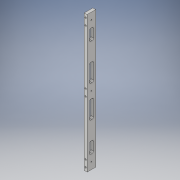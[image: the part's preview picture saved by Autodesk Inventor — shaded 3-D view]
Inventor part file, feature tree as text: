
AUTODESK INVENTOR PART (.ipt)
format: ipt  version: 2019 (Build 230136000, 136)  size: 211,456 bytes
history: native  units: in
note: dims shown in document units (in); Inventor stores cm internally (conversion verified against a paired STEP export)
features: fillet x16, sketch x4, extrude x2, hole x2
ambient origin geometry x8: Origin, YZ Plane, XZ Plane, XY Plane, X Axis, Y Axis, Z Axis, Center Point
bodies: Solid1 (feature_tree)
feature tree (24):
  extrude  "Extrusion1"  Depth=0.75in
  hole  "Hole1"  [1 undecoded]
  extrude  "Extrusion2"  Depth=5.9055in
  fillet  "Fillet1"  Radius=0.5906in
  fillet  "Fillet2"  Radius=0.375in
  fillet  "Fillet3"  Radius=0.375in
  fillet  "Fillet4"  Radius=5.9055in
  fillet  "Fillet5"  Radius=0.1969in
  fillet  "Fillet6"  Radius=0.1969in
  fillet  "Fillet7"  Radius=1.1811in
  fillet  "Fillet8"  Radius=1.1811in
  fillet  "Fillet9"  Radius=2.1654in
  fillet  "Fillet10"  Radius=3.7402in
  fillet  "Fillet11"  Radius=5.315in
  fillet  "Fillet12"  Radius=2.1654in
  fillet  "Fillet13"  Radius=3.7402in
  fillet  "Fillet14"  Radius=5.315in
  fillet  "Fillet15"  Radius=0.25in
  fillet  "Fillet16"  Radius=0.125in
  hole  "Hole3"  [1 undecoded]
  sketch  "Sketch1"  dims[d0=11.811in d1=0.75in]
  sketch  "Sketch2"  dims[d2=0.25in d3=0.0in d4=0.5906in]
  sketch  "Sketch5"  dims[d5=0.75in d6=0.375in d7=0.5906in d8=0.375in d9=0.375in d10=5.9055in]
  sketch  "Sketch7"  dims[d11=0.097in d12=0.236in d13=0.375in d14=0.25in d15=0.5635in d16=0.346in d17=0.8108in d44=0.1969in d45=0.1969in d46=1.1811in d47=1.1811in d48=2.1654in d49=3.7402in d50=5.315in d51=2.1654in d52=3.7402in d53=5.315in d54=0.25in d55=0.0in d56=0.125in d57=0.125in d58=0.125in d59=0.125in d60=0.125in d61=0.125in d62=0.125in d63=0.125in d64=0.125in d65=0.125in d66=0.125in d67=0.125in d68=0.125in d69=0.125in d70=0.125in d71=0.125in d72=0.2953in d73=0.8858in d74=5.6102in d78=0.2953in d79=0.8858in d82=5.6102in d83=0.25in d84=0.125in d85=0.125in d87=0.125in d88=0.125in d89=0.125in d91=0.125in d92=0.125in d93=0.125in d94=0.13in d95=0.328in d96=0.375in d97=0.25in d98=0.5635in d99=0.484in d100=0.0in]
note: 2 required parameter values undecoded (feature->parameter linkage not recoverable at this tier; creation-order binding heuristic only, values carry confidence <= 0.55)
